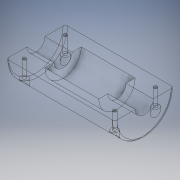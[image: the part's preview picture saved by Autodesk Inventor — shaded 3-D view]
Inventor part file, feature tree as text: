
AUTODESK INVENTOR PART (.ipt)
format: ipt  version: 2018 (Build 220112000, 112)  size: 199,168 bytes
history: native  units: in
note: dims shown in document units (in); Inventor stores cm internally (conversion verified against a paired STEP export)
features: extrude x5, sketch x5, plane x1, fillet x1
ambient origin geometry x8: Origin, YZ Plane, XZ Plane, XY Plane, X Axis, Y Axis, Z Axis, Center Point
bodies: Solid1 (feature_tree)
feature tree (12):
  extrude  "Extrusion1"  Depth=1.0in
  extrude  "Extrusion2"  Depth=0.5in
  extrude  "Extrusion3"  Depth=1.125in
  extrude  "Extrusion4"  Depth=1.5in
  plane  "Work Plane1"
  extrude  "Extrusion5"  Depth=1.5in TaperAngle=0.0deg
  fillet  "Fillet1"  Radius=0.5in
  sketch  "Sketch2"  dims[d0=1.0in d2=0.625in]
  sketch  "Sketch3"  dims[d3=2.9685in d4=0.0in d5=0.5in]
  sketch  "Sketch4"  dims[d7=1.125in d8=1.125in]
  sketch  "Sketch6"  dims[d9=1.5in d10=0.0in d11=0.5in d13=1.125in d14=1.125in d15=0.5in]
  sketch  "Sketch7"  dims[d16=0.5in d17=1.5in d18=0.0in d45=0.5in d46=0.5in d47=0.5in d48=0.5in d49=0.5in d50=0.5in d51=0.5in d52=0.5in d53=0.19in d54=0.19in d55=0.19in d56=0.19in d57=1.5in d58=0.0in d59=-1.1196in d60=0.4in d61=0.4in d62=0.4in d63=0.4in d64=0.2in d65=0.5in d66=0.0in d67=0.0in d68=1.625in d69=1.625in d70=1.625in d71=0.125in]
